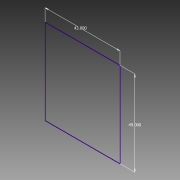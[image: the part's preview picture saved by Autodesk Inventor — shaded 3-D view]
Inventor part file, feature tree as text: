
AUTODESK INVENTOR PART (.ipt)
format: ipt  version: 2013 (Build 170138000, 138)  size: 60,416 bytes
history: native  units: in
note: dims shown in document units (in); Inventor stores cm internally (conversion verified against a paired STEP export)
features: sketch x1
ambient origin geometry x8: Origin, YZ Plane, XZ Plane, XY Plane, X Axis, Y Axis, Z Axis, Center Point
feature tree (1):
  sketch  "Sketch1"  dims[d0=43.0in d1=49.0in]
